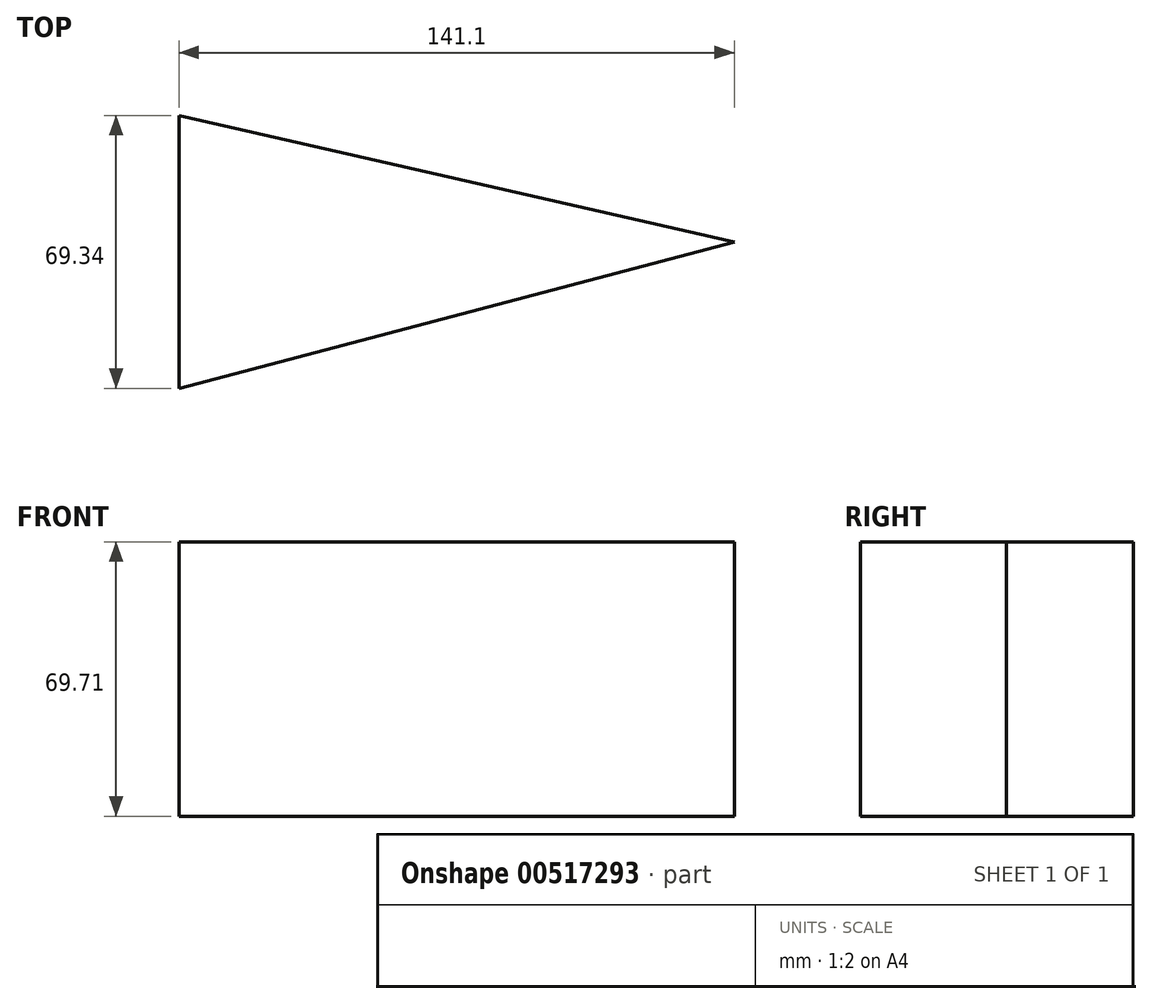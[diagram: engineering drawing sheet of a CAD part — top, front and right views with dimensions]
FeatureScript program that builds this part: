
annotation { "Feature Type Name" : "Feature", "Feature Type Description" : "" }
export const myFeature = defineFeature(function(context is Context, id is Id, definition is map)
    precondition{}
    {
        {
            var Q0;
            Q0=qCreatedBy(makeId("Front.planeOp"),FACE);
            var sketch = newSketch(context, id + "F0", { "sketchPlane" : qUnion([Q0])});
            skLineSegment(sketch, "E0.bottom", {"start": v(-56.74, 12.22) * mm, "end": v(84.36, 12.22) * mm});
            skLineSegment(sketch, "E0.top", {"start": v(-56.74, -57.5) * mm, "end": v(84.36, -57.5) * mm});
            skLineSegment(sketch, "E0.left", {"start": v(-56.74, 12.22) * mm, "end": v(-56.74, -57.5) * mm});
            skLineSegment(sketch, "E0.right", {"start": v(84.36, 12.22) * mm, "end": v(84.36, -57.5) * mm});
            skSolve(sketch);
        }
        {
            var Q0;
            Q0 = qSketchRegion(id + "F0", true);
            extrude(context, id + "F1", {"entities" : qUnion([Q0]), "depth" : 69.34 * mm, "offsetDistance" : 25.4 * mm});
        }
        {
            var Q0;
            Q0=makeQuery(id+"F1.opExtrude","SWEPT_FACE",FACE,{"disambiguationData":[OSD([sQuery(id+"F0.wireOp",EDGE,"E0.bottom")])]});
            var sketch = newSketch(context, id + "F2", { "sketchPlane" : qUnion([Q0])});
            skLineSegment(sketch, "E1", {"start": v(-56.74, -69.34) * mm, "end": v(84.36, -32.19) * mm});
            skLineSegment(sketch, "E2", {"start": v(84.36, -32.19) * mm, "end": v(84.36, -69.34) * mm});
            skLineSegment(sketch, "E3", {"start": v(84.36, -69.34) * mm, "end": v(-56.74, -69.34) * mm});
            skLineSegment(sketch, "E4", {"start": v(-56.74, 0) * mm, "end": v(84.36, -32.19) * mm});
            skLineSegment(sketch, "E5", {"start": v(84.36, 0) * mm, "end": v(-56.74, 0) * mm});
            skSolve(sketch);
        }
        {
            var Q0;
            Q0 = qSketchRegion(id + "F2", true);
            extrude(context, id + "F3", {"entities" : qUnion([Q0]), "operationType" : NewBodyOperationType.REMOVE, "oppositeDirection" : true, "depth" : 115.06 * mm, "offsetDistance" : 25.4 * mm});
        }
        {
            var Q0;
            Q0=makeQuery(id+"F1.opExtrude","SWEPT_FACE",FACE,{"disambiguationData":[OSD([sQuery(id+"F0.wireOp",EDGE,"E0.bottom")])]});
            var sketch = newSketch(context, id + "F4", { "sketchPlane" : qUnion([Q0])});
            skLineSegment(sketch, "E6", {"start": v(-56.74, 0) * mm, "end": v(84.36, -32.19) * mm});
            skLineSegment(sketch, "E7", {"start": v(84.36, -32.19) * mm, "end": v(84.36, 0) * mm});
            skLineSegment(sketch, "E8", {"start": v(84.36, 0) * mm, "end": v(-56.74, 0) * mm});
            skSolve(sketch);
        }
        {
            var Q0;
            Q0 = qSketchRegion(id + "F4", true);
            extrude(context, id + "F5", {"entities" : qUnion([Q0]), "operationType" : NewBodyOperationType.REMOVE, "oppositeDirection" : true, "depth" : 121.16 * mm, "offsetDistance" : 25.4 * mm});
        }
    });
